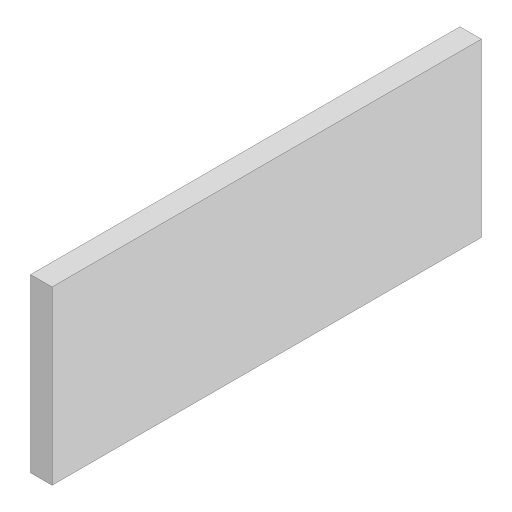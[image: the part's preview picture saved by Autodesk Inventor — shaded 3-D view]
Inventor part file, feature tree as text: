
AUTODESK INVENTOR PART (.ipt)
format: ipt  version: 2023 (Build 270158000, 158)  size: 78,336 bytes
history: native  units: in
note: dims shown in document units (in); Inventor stores cm internally (conversion verified against a paired STEP export)
features: extrude x1, sketch x1
ambient origin geometry x8: Origin, YZ Plane, XZ Plane, XY Plane, X Axis, Y Axis, Z Axis, Center Point
bodies: Solid1 (feature_tree)
feature tree (2):
  extrude  "Extrusion1"  Depth=78.7402in
  sketch  "Sketch1"  dims[d0=9.8425in d1=78.7402in d2=196.8504in d3=0.0in]
